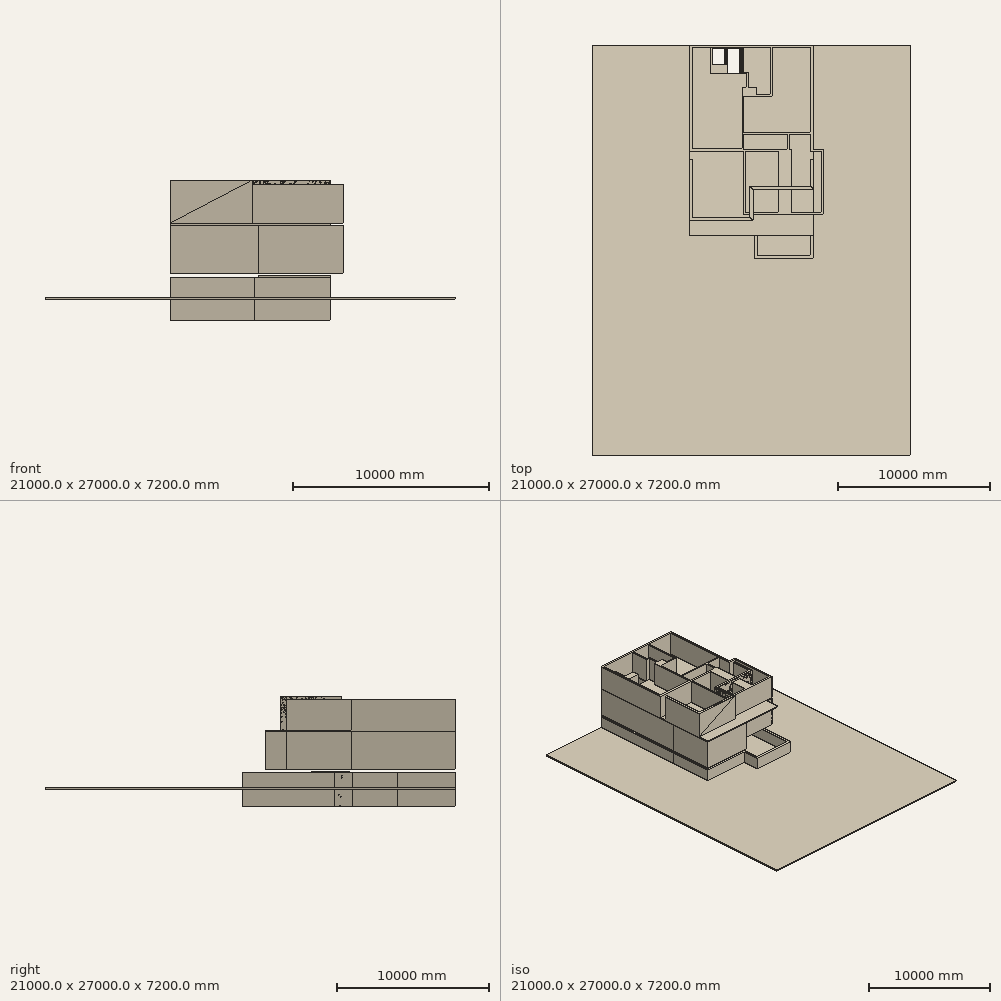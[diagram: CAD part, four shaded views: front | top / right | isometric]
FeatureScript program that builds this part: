
annotation { "Feature Type Name" : "Feature", "Feature Type Description" : "" }
export const myFeature = defineFeature(function(context is Context, id is Id, definition is map)
    precondition{}
    {
        {
            var Q0;
            Q0=qCreatedBy(makeId("Top.planeOp"),FACE);
            var sketch = newSketch(context, id + "F0", { "sketchPlane" : qUnion([Q0])});
            skLineSegment(sketch, "E0", {"start": v(-4100, -4250) * mm, "end": v(-4100, 4250) * mm});
            skLineSegment(sketch, "E1", {"start": v(-4100, 4250) * mm, "end": v(4100, 4250) * mm});
            skLineSegment(sketch, "E2", {"start": v(4100, 4250) * mm, "end": v(4100, -2750) * mm});
            skLineSegment(sketch, "E3", {"start": v(4100, -2750) * mm, "end": v(400, -2750) * mm});
            skLineSegment(sketch, "E4", {"start": v(400, -2750) * mm, "end": v(400, -4250) * mm});
            skLineSegment(sketch, "E5", {"start": v(400, -4250) * mm, "end": v(-4100, -4250) * mm});
            skLineSegment(sketch, "E6", {"start": v(-3950, -4100) * mm, "end": v(-3950, 4100) * mm});
            skLineSegment(sketch, "E7", {"start": v(-3950, 4100) * mm, "end": v(3900, 4100) * mm});
            skLineSegment(sketch, "E8", {"start": v(3900, 4100) * mm, "end": v(3900, -2600) * mm});
            skLineSegment(sketch, "E9", {"start": v(3900, -2600) * mm, "end": v(250, -2600) * mm});
            skLineSegment(sketch, "E10", {"start": v(250, -2600) * mm, "end": v(250, -4100) * mm});
            skLineSegment(sketch, "E11", {"start": v(250, -4100) * mm, "end": v(-3950, -4100) * mm});
            skLineSegment(sketch, "E12.bottom", {"start": v(-2750, 4100) * mm, "end": v(-2650, 4100) * mm});
            skLineSegment(sketch, "E12.top", {"start": v(-2750, 2100) * mm, "end": v(-2650, 2100) * mm});
            skLineSegment(sketch, "E12.left", {"start": v(-2750, 4100) * mm, "end": v(-2750, 2100) * mm});
            skLineSegment(sketch, "E12.right", {"start": v(-2650, 4100) * mm, "end": v(-2650, 2100) * mm});
            skLineSegment(sketch, "E13", {"start": v(-3950, 3300) * mm, "end": v(-2750, 3300) * mm});
            skLineSegment(sketch, "E14", {"start": v(-3950, 3200) * mm, "end": v(-2750, 3200) * mm});
            skLineSegment(sketch, "E15", {"start": v(-3950, 800) * mm, "end": v(-650, 800) * mm});
            skLineSegment(sketch, "E16", {"start": v(-650, 800) * mm, "end": v(-650, 2100) * mm});
            skLineSegment(sketch, "E17", {"start": v(-650, 2100) * mm, "end": v(-1650, 2100) * mm});
            skLineSegment(sketch, "E18", {"start": v(-1650, 2100) * mm, "end": v(-1650, 4100) * mm});
            skLineSegment(sketch, "E19", {"start": v(-1650, 4100) * mm, "end": v(-1550, 4100) * mm});
            skLineSegment(sketch, "E20", {"start": v(-1550, 4100) * mm, "end": v(-1550, 2200) * mm});
            skLineSegment(sketch, "E21", {"start": v(-1550, 2200) * mm, "end": v(-550, 2200) * mm});
            skLineSegment(sketch, "E22", {"start": v(-550, 2200) * mm, "end": v(-550, 700) * mm});
            skLineSegment(sketch, "E23", {"start": v(-550, 700) * mm, "end": v(-3950, 700) * mm});
            skLineSegment(sketch, "E24", {"start": v(-3950, 700) * mm, "end": v(-3950, 800) * mm});
            skLineSegment(sketch, "E25", {"start": v(-550, 2200) * mm, "end": v(-550, 4100) * mm});
            skLineSegment(sketch, "E26", {"start": v(-650, 4100) * mm, "end": v(-650, 2200) * mm});
            skLineSegment(sketch, "E27", {"start": v(-550, 700) * mm, "end": v(3900, 700) * mm});
            skLineSegment(sketch, "E28", {"start": v(3900, 800) * mm, "end": v(-550, 800) * mm});
            skLineSegment(sketch, "E29", {"start": v(-650, 700) * mm, "end": v(-650, 400) * mm});
            skLineSegment(sketch, "E30", {"start": v(-650, 400) * mm, "end": v(0, -200) * mm});
            skLineSegment(sketch, "E31", {"start": v(0, -200) * mm, "end": v(300, -200) * mm});
            skLineSegment(sketch, "E32", {"start": v(300, -200) * mm, "end": v(300, 0) * mm});
            skLineSegment(sketch, "E33", {"start": v(1800, 4100) * mm, "end": v(1800, 800) * mm});
            skLineSegment(sketch, "E34", {"start": v(1900, 4100) * mm, "end": v(1900, 800) * mm});
            skLineSegment(sketch, "E35", {"start": v(300, 0) * mm, "end": v(300, 1300) * mm});
            skLineSegment(sketch, "E36", {"start": v(300, 1300) * mm, "end": v(-550, 1300) * mm});
            skLineSegment(sketch, "E37", {"start": v(-550, -4250) * mm, "end": v(-550, -6900) * mm});
            skLineSegment(sketch, "E38", {"start": v(-550, -6900) * mm, "end": v(4750, -6900) * mm});
            skLineSegment(sketch, "E39", {"start": v(4750, -6900) * mm, "end": v(4750, -2600) * mm});
            skLineSegment(sketch, "E40", {"start": v(4750, -2600) * mm, "end": v(4100, -2600) * mm});
            skLineSegment(sketch, "E41", {"start": v(4100, -2750) * mm, "end": v(4600, -2750) * mm});
            skLineSegment(sketch, "E42", {"start": v(4600, -2750) * mm, "end": v(4600, -6750) * mm});
            skLineSegment(sketch, "E43", {"start": v(4600, -6750) * mm, "end": v(-400, -6750) * mm});
            skLineSegment(sketch, "E44", {"start": v(-400, -6750) * mm, "end": v(-400, -4250) * mm});
            skSolve(sketch);
        }
        {
            var Q0;
            Q0=makeQuery(id+"F0.imprint","IMPRINT",FACE,{"disambiguationData":[TD([[makeQuery(id+"F0.imprint","IMPRINT",EDGE,{"derivedFrom":sQuery(id+"F0.wireOp",EDGE,"E15")}),-1.0]])]});
            var Q1;
            {var subQ3=sQuery(id+"F0.wireOp",EDGE,"E36");Q1=makeQuery(id+"F0.imprint","IMPRINT",FACE,{"disambiguationData":[TD([[makeQuery(id+"F0.imprint","IMPRINT",EDGE,{"derivedFrom":subQ3}),1.0]])]});}
            var Q2;
            {var subQ1=sQuery(id+"F0.wireOp",EDGE,"E22");var subQ3=sQuery(id+"F0.wireOp",EDGE,"E28");var subQ4=makeQuery(id+"F0.imprint","INTERSECT",VERTEX,{"derivedFrom":[subQ1,subQ3]});Q2=makeQuery(id+"F0.imprint","IMPRINT",FACE,{"disambiguationData":[TD([[makeQuery(id+"F0.imprint","IMPRINT",EDGE,{"disambiguationData":[TD([[subQ4,1.0]])],"derivedFrom":subQ3}),1.0]])]});}
            var Q3;
            {var subQ0=sQuery(id+"F0.wireOp",EDGE,"E29");Q3=makeQuery(id+"F0.imprint","IMPRINT",FACE,{"disambiguationData":[TD([[makeQuery(id+"F0.imprint","IMPRINT",EDGE,{"derivedFrom":subQ0}),1.0]])]});}
            var Q4;
            {var subQ3=sQuery(id+"F0.wireOp",EDGE,"E8");var subQ6=sQuery(id+"F0.wireOp",EDGE,"E27");var subQ9=makeQuery(id+"F0.imprint","INTERSECT",VERTEX,{"derivedFrom":[subQ3,subQ6]});Q4=makeQuery(id+"F0.imprint","IMPRINT",FACE,{"disambiguationData":[TD([[makeQuery(id+"F0.imprint","IMPRINT",EDGE,{"disambiguationData":[TD([[subQ9,1.0]])],"derivedFrom":subQ3}),-1.0]])]});}
            var Q5;
            {var subQ0=sQuery(id+"F0.wireOp",EDGE,"E33");Q5=makeQuery(id+"F0.imprint","IMPRINT",FACE,{"disambiguationData":[TD([[makeQuery(id+"F0.imprint","IMPRINT",EDGE,{"derivedFrom":subQ0}),1.0]])]});}
            var Q6;
            Q6=makeQuery(id+"F0.imprint","IMPRINT",FACE,{"disambiguationData":[TD([[makeQuery(id+"F0.imprint","IMPRINT",EDGE,{"derivedFrom":sQuery(id+"F0.wireOp",EDGE,"E0")}),-1.0]])]});
            var Q7;
            {var subQ0=sQuery(id+"F0.wireOp",EDGE,"E13");Q7=makeQuery(id+"F0.imprint","IMPRINT",FACE,{"disambiguationData":[TD([[makeQuery(id+"F0.imprint","IMPRINT",EDGE,{"derivedFrom":subQ0}),-1.0]])]});}
            var Q8;
            {var subQ3=sQuery(id+"F0.wireOp",EDGE,"E12.bottom");Q8=makeQuery(id+"F0.imprint","IMPRINT",FACE,{"disambiguationData":[TD([[makeQuery(id+"F0.imprint","IMPRINT",EDGE,{"derivedFrom":subQ3}),-1.0]])]});}
            var Q9;
            {var subQ0=sQuery(id+"F0.wireOp",EDGE,"E25");Q9=makeQuery(id+"F0.imprint","IMPRINT",FACE,{"disambiguationData":[TD([[makeQuery(id+"F0.imprint","IMPRINT",EDGE,{"derivedFrom":subQ0}),1.0]])]});}
            var Q10;
            {var subQ0=sQuery(id+"F0.wireOp",EDGE,"E37");Q10=makeQuery(id+"F0.imprint","IMPRINT",FACE,{"disambiguationData":[TD([[makeQuery(id+"F0.imprint","IMPRINT",EDGE,{"derivedFrom":subQ0}),1.0]])]});}
            extrude(context, id + "F1", {"entities" : qUnion([Q0, Q1, Q2, Q3, Q4, Q5, Q6, Q7, Q8, Q9, Q10]), "depth" : 2500 * mm, "offsetDistance" : 25 * mm});
        }
        {
            var Q0;
            Q0=makeQuery(id+"F1.opExtrude","CAP_FACE",FACE,{"disambiguationData":[OSD([sQuery(id+"F0.wireOp",EDGE,"E0"),sQuery(id+"F0.wireOp",EDGE,"E1"),sQuery(id+"F0.wireOp",EDGE,"E2"),sQuery(id+"F0.wireOp",EDGE,"E3"),sQuery(id+"F0.wireOp",EDGE,"E4"),sQuery(id+"F0.wireOp",EDGE,"E5"),sQuery(id+"F0.wireOp",EDGE,"E6"),sQuery(id+"F0.wireOp",EDGE,"E7"),sQuery(id+"F0.wireOp",EDGE,"E8"),sQuery(id+"F0.wireOp",EDGE,"E9"),sQuery(id+"F0.wireOp",EDGE,"E10"),sQuery(id+"F0.wireOp",EDGE,"E11"),sQuery(id+"F0.wireOp",EDGE,"E12.top"),sQuery(id+"F0.wireOp",EDGE,"E12.left"),sQuery(id+"F0.wireOp",EDGE,"E12.right"),sQuery(id+"F0.wireOp",EDGE,"E13"),sQuery(id+"F0.wireOp",EDGE,"E14"),sQuery(id+"F0.wireOp",EDGE,"E15"),sQuery(id+"F0.wireOp",EDGE,"E16"),sQuery(id+"F0.wireOp",EDGE,"E17"),sQuery(id+"F0.wireOp",EDGE,"E18"),sQuery(id+"F0.wireOp",EDGE,"E20"),sQuery(id+"F0.wireOp",EDGE,"E21"),sQuery(id+"F0.wireOp",EDGE,"E22"),sQuery(id+"F0.wireOp",EDGE,"E23"),sQuery(id+"F0.wireOp",EDGE,"E25"),sQuery(id+"F0.wireOp",EDGE,"E26"),sQuery(id+"F0.wireOp",EDGE,"E27"),sQuery(id+"F0.wireOp",EDGE,"E28"),sQuery(id+"F0.wireOp",EDGE,"E29"),sQuery(id+"F0.wireOp",EDGE,"E30"),sQuery(id+"F0.wireOp",EDGE,"E31"),sQuery(id+"F0.wireOp",EDGE,"E32")])],"isStart":true});
            cPlane(context, id + "F2", {"entities" : qUnion([Q0]), "cplaneType" : CPlaneType.OFFSET, "offset" : 200 * mm, "width" : 150 * mm, "height" : 150 * mm});
        }
        {
            var Q0;
            Q0=qCreatedBy(id+"F2.planeOp",FACE);
            var sketch = newSketch(context, id + "F3", { "sketchPlane" : qUnion([Q0])});
            skLineSegment(sketch, "E45.bottom", {"start": v(400, 2750) * mm, "end": v(4100, 2750) * mm});
            skLineSegment(sketch, "E45.top", {"start": v(400, 5250) * mm, "end": v(4100, 5250) * mm});
            skLineSegment(sketch, "E45.left", {"start": v(400, 2750) * mm, "end": v(400, 5250) * mm});
            skLineSegment(sketch, "E45.right", {"start": v(4100, 2750) * mm, "end": v(4100, 5250) * mm});
            skSolve(sketch);
        }
        {
            var Q0;
            Q0=makeQuery(id+"F3.imprint","IMPRINT",FACE,{"disambiguationData":[TD([[makeQuery(id+"F3.imprint","IMPRINT",EDGE,{"derivedFrom":sQuery(id+"F3.wireOp",EDGE,"E45.bottom")}),1.0]])]});
            extrude(context, id + "F4", {"entities" : qUnion([Q0]), "oppositeDirection" : true, "depth" : 100 * mm, "offsetDistance" : 25 * mm});
        }
        {
            var Q0;
            Q0=makeQuery(id+"F1.opExtrude","CAP_FACE",FACE,{"disambiguationData":[OSD([sQuery(id+"F0.wireOp",EDGE,"E0"),sQuery(id+"F0.wireOp",EDGE,"E1"),sQuery(id+"F0.wireOp",EDGE,"E2"),sQuery(id+"F0.wireOp",EDGE,"E3"),sQuery(id+"F0.wireOp",EDGE,"E4"),sQuery(id+"F0.wireOp",EDGE,"E5"),sQuery(id+"F0.wireOp",EDGE,"E6"),sQuery(id+"F0.wireOp",EDGE,"E7"),sQuery(id+"F0.wireOp",EDGE,"E8"),sQuery(id+"F0.wireOp",EDGE,"E9"),sQuery(id+"F0.wireOp",EDGE,"E10"),sQuery(id+"F0.wireOp",EDGE,"E11"),sQuery(id+"F0.wireOp",EDGE,"E12.top"),sQuery(id+"F0.wireOp",EDGE,"E12.left"),sQuery(id+"F0.wireOp",EDGE,"E12.right"),sQuery(id+"F0.wireOp",EDGE,"E13"),sQuery(id+"F0.wireOp",EDGE,"E14"),sQuery(id+"F0.wireOp",EDGE,"E15"),sQuery(id+"F0.wireOp",EDGE,"E16"),sQuery(id+"F0.wireOp",EDGE,"E17"),sQuery(id+"F0.wireOp",EDGE,"E18"),sQuery(id+"F0.wireOp",EDGE,"E20"),sQuery(id+"F0.wireOp",EDGE,"E21"),sQuery(id+"F0.wireOp",EDGE,"E22"),sQuery(id+"F0.wireOp",EDGE,"E23"),sQuery(id+"F0.wireOp",EDGE,"E25"),sQuery(id+"F0.wireOp",EDGE,"E26"),sQuery(id+"F0.wireOp",EDGE,"E27"),sQuery(id+"F0.wireOp",EDGE,"E28"),sQuery(id+"F0.wireOp",EDGE,"E29"),sQuery(id+"F0.wireOp",EDGE,"E30"),sQuery(id+"F0.wireOp",EDGE,"E31"),sQuery(id+"F0.wireOp",EDGE,"E32")])],"isStart":false});
            cPlane(context, id + "F5", {"entities" : qUnion([Q0]), "cplaneType" : CPlaneType.OFFSET, "offset" : 0 * mm, "width" : 150 * mm, "height" : 150 * mm});
        }
        {
            var Q0;
            Q0=qCreatedBy(id+"F5.planeOp",FACE);
            var sketch = newSketch(context, id + "F6", { "sketchPlane" : qUnion([Q0])});
            skLineSegment(sketch, "E46.bottom", {"start": v(-4100, 4250) * mm, "end": v(4100, 4250) * mm});
            skLineSegment(sketch, "E46.top", {"start": v(-4100, -4450) * mm, "end": v(4100, -4450) * mm});
            skLineSegment(sketch, "E46.left", {"start": v(-4100, 4250) * mm, "end": v(-4100, -4450) * mm});
            skLineSegment(sketch, "E46.right", {"start": v(4100, 4250) * mm, "end": v(4100, -4450) * mm});
            skLineSegment(sketch, "E47.bottom", {"start": v(-2600, 4100) * mm, "end": v(-600, 4100) * mm});
            skLineSegment(sketch, "E47.top", {"start": v(-2600, 2400) * mm, "end": v(-600, 2400) * mm});
            skLineSegment(sketch, "E47.left", {"start": v(-2600, 4100) * mm, "end": v(-2600, 2400) * mm});
            skLineSegment(sketch, "E47.right", {"start": v(-600, 4100) * mm, "end": v(-600, 2400) * mm});
            skSolve(sketch);
        }
        {
            var Q0;
            Q0=makeQuery(id+"F6.imprint","IMPRINT",FACE,{"disambiguationData":[TD([[makeQuery(id+"F6.imprint","IMPRINT",EDGE,{"derivedFrom":sQuery(id+"F6.wireOp",EDGE,"E46.bottom")}),-1.0]])]});
            extrude(context, id + "F7", {"entities" : qUnion([Q0]), "depth" : 100 * mm, "offsetDistance" : 25 * mm});
        }
        {
            var Q0;
            Q0=makeQuery(id+"F7.opExtrude","CAP_FACE",FACE,{"disambiguationData":[OSD([sQuery(id+"F6.wireOp",EDGE,"E46.bottom"),sQuery(id+"F6.wireOp",EDGE,"E46.top"),sQuery(id+"F6.wireOp",EDGE,"E46.left"),sQuery(id+"F6.wireOp",EDGE,"E46.right")])],"isStart":false});
            var sketch = newSketch(context, id + "F8", { "sketchPlane" : qUnion([Q0])});
            skLineSegment(sketch, "E48", {"start": v(-4100, -2750) * mm, "end": v(-400, -2750) * mm});
            skLineSegment(sketch, "E49", {"start": v(-2600, 4100) * mm, "end": v(-3900, 4100) * mm});
            skLineSegment(sketch, "E50", {"start": v(-3900, 4100) * mm, "end": v(-3900, -2550) * mm});
            skLineSegment(sketch, "E51", {"start": v(-3900, -2550) * mm, "end": v(-500, -2550) * mm});
            skLineSegment(sketch, "E52", {"start": v(3900, -2550) * mm, "end": v(3900, 4100) * mm});
            skLineSegment(sketch, "E53", {"start": v(3900, 4100) * mm, "end": v(-2600, 4100) * mm});
            skLineSegment(sketch, "E54", {"start": v(-2700, 4100) * mm, "end": v(-2700, 2500) * mm});
            skLineSegment(sketch, "E55", {"start": v(-2700, 2500) * mm, "end": v(-3900, 2500) * mm});
            skLineSegment(sketch, "E56", {"start": v(-3900, 2500) * mm, "end": v(-3900, 2400) * mm});
            skLineSegment(sketch, "E57", {"start": v(-3900, 2400) * mm, "end": v(-2600, 2400) * mm});
            skLineSegment(sketch, "E58", {"start": v(-2600, 2400) * mm, "end": v(-2600, 4100) * mm});
            skLineSegment(sketch, "E59", {"start": v(-2600, 4100) * mm, "end": v(-2700, 4100) * mm});
            skLineSegment(sketch, "E60", {"start": v(-600, 4100) * mm, "end": v(-600, 2400) * mm});
            skLineSegment(sketch, "E61", {"start": v(-600, 2400) * mm, "end": v(1350, 2400) * mm});
            skLineSegment(sketch, "E62", {"start": v(1350, 2400) * mm, "end": v(1350, 4100) * mm});
            skLineSegment(sketch, "E63", {"start": v(1350, 4100) * mm, "end": v(-600, 4100) * mm});
            skLineSegment(sketch, "E64", {"start": v(-500, 4100) * mm, "end": v(-500, 2500) * mm});
            skLineSegment(sketch, "E65", {"start": v(-500, 2500) * mm, "end": v(1250, 2500) * mm});
            skLineSegment(sketch, "E66", {"start": v(1250, 2500) * mm, "end": v(1250, 4100) * mm});
            skLineSegment(sketch, "E67", {"start": v(1350, 2400) * mm, "end": v(1350, 1000) * mm});
            skLineSegment(sketch, "E68", {"start": v(1350, 1000) * mm, "end": v(3900, 1000) * mm});
            skLineSegment(sketch, "E69", {"start": v(3900, 1000) * mm, "end": v(3900, 900) * mm});
            skLineSegment(sketch, "E70", {"start": v(3900, 900) * mm, "end": v(1250, 900) * mm});
            skLineSegment(sketch, "E71", {"start": v(1250, 900) * mm, "end": v(1250, 2400) * mm});
            skLineSegment(sketch, "E72", {"start": v(1250, 2400) * mm, "end": v(1350, 2400) * mm});
            skLineSegment(sketch, "E73", {"start": v(1250, 900) * mm, "end": v(-500, 900) * mm});
            skLineSegment(sketch, "E74", {"start": v(-500, 900) * mm, "end": v(-500, -2550) * mm});
            skLineSegment(sketch, "E75", {"start": v(-500, -2550) * mm, "end": v(-600, -2550) * mm});
            skLineSegment(sketch, "E76", {"start": v(-600, -2550) * mm, "end": v(-600, 1000) * mm});
            skLineSegment(sketch, "E77", {"start": v(-600, 1000) * mm, "end": v(1250, 1000) * mm});
            skLineSegment(sketch, "E78", {"start": v(1250, 1000) * mm, "end": v(1250, 900) * mm});
            skLineSegment(sketch, "E79", {"start": v(-3900, -440) * mm, "end": v(-3900, -340) * mm});
            skLineSegment(sketch, "E80", {"start": v(-2600, 2400) * mm, "end": v(-1600, 2400) * mm});
            skLineSegment(sketch, "E81", {"start": v(-4100, -2750) * mm, "end": v(-4100, 4250) * mm});
            skLineSegment(sketch, "E82", {"start": v(-4100, 4250) * mm, "end": v(4100, 4250) * mm});
            skLineSegment(sketch, "E83", {"start": v(4100, 4250) * mm, "end": v(4100, -2750) * mm});
            skLineSegment(sketch, "E84", {"start": v(-1600, 2400) * mm, "end": v(-1600, 3000) * mm});
            skLineSegment(sketch, "E85", {"start": v(-1600, 3000) * mm, "end": v(-2600, 3000) * mm});
            skLineSegment(sketch, "E86", {"start": v(-600, 1000) * mm, "end": v(-600, 1500) * mm});
            skLineSegment(sketch, "E87", {"start": v(-600, 1500) * mm, "end": v(350, 1500) * mm});
            skLineSegment(sketch, "E88", {"start": v(350, 1500) * mm, "end": v(350, 1000) * mm});
            skPoint(sketch, "E89.endSnap0", {"position": v(375, 900) * mm});
            skLineSegment(sketch, "E90", {"start": v(4100, -2750) * mm, "end": v(4600, -2750) * mm});
            skLineSegment(sketch, "E91", {"start": v(4600, -2750) * mm, "end": v(4600, -6750) * mm});
            skLineSegment(sketch, "E92", {"start": v(4600, -6750) * mm, "end": v(-400, -6750) * mm});
            skLineSegment(sketch, "E93", {"start": v(-400, -6750) * mm, "end": v(-400, -2750) * mm});
            skLineSegment(sketch, "E94", {"start": v(-550, -6900) * mm, "end": v(4750, -6900) * mm});
            skLineSegment(sketch, "E95", {"start": v(4750, -6900) * mm, "end": v(4750, -2600) * mm});
            skLineSegment(sketch, "E96", {"start": v(4750, -2600) * mm, "end": v(4100, -2600) * mm});
            skLineSegment(sketch, "E97", {"start": v(4100, -2600) * mm, "end": v(4100, -2750) * mm});
            skLineSegment(sketch, "E98", {"start": v(-550, -6900) * mm, "end": v(-550, -2750) * mm});
            skLineSegment(sketch, "E99", {"start": v(1750, -6750) * mm, "end": v(1750, -2600) * mm});
            skLineSegment(sketch, "E100", {"start": v(2650, -2600) * mm, "end": v(2650, -6750) * mm});
            skLineSegment(sketch, "E101", {"start": v(3900, -1600) * mm, "end": v(-500, -1600) * mm});
            skLineSegment(sketch, "E102", {"start": v(-500, -1450) * mm, "end": v(3900, -1450) * mm});
            skLineSegment(sketch, "E103", {"start": v(2200, -6750) * mm, "end": v(2200, -2600) * mm});
            skLineSegment(sketch, "E104", {"start": v(1750, -2600) * mm, "end": v(2650, -2600) * mm});
            skLineSegment(sketch, "E105", {"start": v(3900, -2550) * mm, "end": v(3900, -2750) * mm});
            skLineSegment(sketch, "E106", {"start": v(3900, -2750) * mm, "end": v(4100, -2750) * mm});
            skLineSegment(sketch, "E107", {"start": v(-500, -2550) * mm, "end": v(-500, -2750) * mm});
            skLineSegment(sketch, "E108", {"start": v(-400, -2750) * mm, "end": v(1750, -2750) * mm});
            skLineSegment(sketch, "E109", {"start": v(1750, -2600) * mm, "end": v(-500, -2600) * mm});
            skLineSegment(sketch, "E110", {"start": v(2377.07, -1600) * mm, "end": v(2377.07, -2600) * mm});
            skLineSegment(sketch, "E111", {"start": v(2527.07, -1600) * mm, "end": v(2527.07, -2600) * mm});
            skLineSegment(sketch, "E112", {"start": v(1350, 1000) * mm, "end": v(1350, 900) * mm});
            skLineSegment(sketch, "E113", {"start": v(-300, 2400) * mm, "end": v(-300, 1500) * mm});
            skLineSegment(sketch, "E114", {"start": v(-200, 2400) * mm, "end": v(-200, 1500) * mm});
            skLineSegment(sketch, "E115", {"start": v(1250, 2500) * mm, "end": v(1250, 2400) * mm});
            skLineSegment(sketch, "E116", {"start": v(-500, 2500) * mm, "end": v(-500, 2400) * mm});
            skLineSegment(sketch, "E117", {"start": v(-200, 2400) * mm, "end": v(-200, 2500) * mm});
            skLineSegment(sketch, "E118", {"start": v(-2700, 2500) * mm, "end": v(-2700, 2400) * mm});
            skSolve(sketch);
        }
        {
            var Q0;
            {var subQ18=sQuery(id+"F8.wireOp",EDGE,"E49");Q0=makeQuery(id+"F8.imprint","IMPRINT",FACE,{"disambiguationData":[TD([[makeQuery(id+"F8.imprint","IMPRINT",EDGE,{"derivedFrom":subQ18}),-1.0]])]});}
            var Q1;
            Q1=makeQuery(id+"F8.imprint","IMPRINT",FACE,{"disambiguationData":[TD([[makeQuery(id+"F8.imprint","IMPRINT",EDGE,{"derivedFrom":sQuery(id+"F8.wireOp",EDGE,"E90")}),1.0]])]});
            var Q2;
            {var subQ1=sQuery(id+"F8.wireOp",EDGE,"E48");var subQ3=sQuery(id+"F8.wireOp",EDGE,"E98");var subQ4=makeQuery(id+"F8.imprint","INTERSECT",VERTEX,{"derivedFrom":[subQ1,subQ3]});Q2=makeQuery(id+"F8.imprint","IMPRINT",FACE,{"disambiguationData":[TD([[makeQuery(id+"F8.imprint","IMPRINT",EDGE,{"disambiguationData":[TD([[subQ4,1.0]])],"derivedFrom":subQ3}),-1.0]])]});}
            var Q3;
            {var subQ2=sQuery(id+"F8.wireOp",EDGE,"E108");Q3=makeQuery(id+"F8.imprint","IMPRINT",FACE,{"disambiguationData":[TD([[makeQuery(id+"F8.imprint","IMPRINT",EDGE,{"derivedFrom":subQ2}),1.0]])]});}
            var Q4;
            {var subQ1=sQuery(id+"F8.wireOp",EDGE,"E99");var subQ5=makeQuery(id+"F8.imprint","INTERSECT",VERTEX,{"derivedFrom":[subQ1,sQuery(id+"F8.wireOp",EDGE,"E108")]});Q4=makeQuery(id+"F8.imprint","IMPRINT",FACE,{"disambiguationData":[TD([[makeQuery(id+"F8.imprint","IMPRINT",EDGE,{"disambiguationData":[TD([[subQ5,1.0]])],"derivedFrom":subQ1}),-1.0]])]});}
            var Q5;
            {var subQ0=sQuery(id+"F8.wireOp",EDGE,"E104");var subQ1=sQuery(id+"F8.wireOp",EDGE,"E100");var subQ2=makeQuery(id+"F8.imprint","INTERSECT",VERTEX,{"derivedFrom":[subQ1,subQ0]});Q5=makeQuery(id+"F8.imprint","IMPRINT",FACE,{"disambiguationData":[TD([[makeQuery(id+"F8.imprint","IMPRINT",EDGE,{"disambiguationData":[TD([[subQ2,-1.0]])],"derivedFrom":subQ1}),-1.0]])]});}
            var Q6;
            {var subQ0=sQuery(id+"F8.wireOp",EDGE,"E99");var subQ1=sQuery(id+"F8.wireOp",EDGE,"E92");var subQ2=makeQuery(id+"F8.imprint","INTERSECT",VERTEX,{"derivedFrom":[subQ1,subQ0]});Q6=makeQuery(id+"F8.imprint","IMPRINT",FACE,{"disambiguationData":[TD([[makeQuery(id+"F8.imprint","IMPRINT",EDGE,{"disambiguationData":[TD([[subQ2,1.0]])],"derivedFrom":subQ1}),-1.0]])]});}
            var Q7;
            {var subQ0=sQuery(id+"F8.wireOp",EDGE,"E100");var subQ1=sQuery(id+"F8.wireOp",EDGE,"E92");var subQ2=makeQuery(id+"F8.imprint","INTERSECT",VERTEX,{"derivedFrom":[subQ1,subQ0]});Q7=makeQuery(id+"F8.imprint","IMPRINT",FACE,{"disambiguationData":[TD([[makeQuery(id+"F8.imprint","IMPRINT",EDGE,{"disambiguationData":[TD([[subQ2,-1.0]])],"derivedFrom":subQ1}),-1.0]])]});}
            var Q8;
            {var subQ4=sQuery(id+"F8.wireOp",EDGE,"E73");Q8=makeQuery(id+"F8.imprint","IMPRINT",FACE,{"disambiguationData":[TD([[makeQuery(id+"F8.imprint","IMPRINT",EDGE,{"derivedFrom":subQ4}),-1.0]])]});}
            var Q9;
            {var subQ5=sQuery(id+"F8.wireOp",EDGE,"E102");Q9=makeQuery(id+"F8.imprint","IMPRINT",FACE,{"disambiguationData":[TD([[makeQuery(id+"F8.imprint","IMPRINT",EDGE,{"derivedFrom":subQ5}),-1.0]])]});}
            var Q10;
            {var subQ0=sQuery(id+"F8.wireOp",EDGE,"E110");Q10=makeQuery(id+"F8.imprint","IMPRINT",FACE,{"disambiguationData":[TD([[makeQuery(id+"F8.imprint","IMPRINT",EDGE,{"derivedFrom":subQ0}),1.0]])]});}
            var Q11;
            Q11=makeQuery(id+"F8.imprint","IMPRINT",FACE,{"disambiguationData":[TD([[makeQuery(id+"F8.imprint","IMPRINT",EDGE,{"derivedFrom":sQuery(id+"F8.wireOp",EDGE,"E67")}),-1.0]])]});
            var Q12;
            {var subQ2=sQuery(id+"F8.wireOp",EDGE,"E60");Q12=makeQuery(id+"F8.imprint","IMPRINT",FACE,{"disambiguationData":[TD([[makeQuery(id+"F8.imprint","IMPRINT",EDGE,{"derivedFrom":subQ2}),1.0]])]});}
            var Q13;
            {var subQ0=sQuery(id+"F8.wireOp",EDGE,"E113");Q13=makeQuery(id+"F8.imprint","IMPRINT",FACE,{"disambiguationData":[TD([[makeQuery(id+"F8.imprint","IMPRINT",EDGE,{"derivedFrom":subQ0}),1.0]])]});}
            var Q14;
            {var subQ3=sQuery(id+"F8.wireOp",EDGE,"E86");Q14=makeQuery(id+"F8.imprint","IMPRINT",FACE,{"disambiguationData":[TD([[makeQuery(id+"F8.imprint","IMPRINT",EDGE,{"derivedFrom":subQ3}),-1.0]])]});}
            var Q15;
            {var subQ0=sQuery(id+"F8.wireOp",EDGE,"E116");Q15=makeQuery(id+"F8.imprint","IMPRINT",FACE,{"disambiguationData":[TD([[makeQuery(id+"F8.imprint","IMPRINT",EDGE,{"derivedFrom":subQ0}),1.0]])]});}
            var Q16;
            {var subQ2=sQuery(id+"F8.wireOp",EDGE,"E62");Q16=makeQuery(id+"F8.imprint","IMPRINT",FACE,{"disambiguationData":[TD([[makeQuery(id+"F8.imprint","IMPRINT",EDGE,{"derivedFrom":subQ2}),1.0]])]});}
            extrude(context, id + "F9", {"entities" : qUnion([Q0, Q1, Q2, Q3, Q4, Q5, Q6, Q7, Q8, Q9, Q10, Q11, Q12, Q13, Q14, Q15, Q16]), "operationType" : NewBodyOperationType.ADD, "depth" : 2000 * mm, "offsetDistance" : 25 * mm});
        }
        {
            var Q0;
            Q0=qCreatedBy(id+"F2.planeOp",FACE);
            cPlane(context, id + "F10", {"entities" : qUnion([Q0]), "cplaneType" : CPlaneType.OFFSET, "offset" : 2200 * mm, "width" : 150 * mm, "height" : 150 * mm});
        }
        {
            var Q0;
            Q0=qCreatedBy(id+"F10.planeOp",FACE);
            var sketch = newSketch(context, id + "F11", { "sketchPlane" : qUnion([Q0])});
            skLineSegment(sketch, "E119.bottom", {"start": v(-4100, -4250) * mm, "end": v(4100, -4250) * mm});
            skLineSegment(sketch, "E119.top", {"start": v(400, 2750) * mm, "end": v(2600, 2750) * mm});
            skLineSegment(sketch, "E119.left", {"start": v(-4100, -4250) * mm, "end": v(-4100, 2750) * mm});
            skLineSegment(sketch, "E119.right", {"start": v(4100, -4250) * mm, "end": v(4100, -450) * mm});
            skLineSegment(sketch, "E120", {"start": v(4100, -450) * mm, "end": v(2600, -450) * mm});
            skLineSegment(sketch, "E121", {"start": v(2600, -450) * mm, "end": v(2600, 2750) * mm});
            skLineSegment(sketch, "E122", {"start": v(-3900, -4050) * mm, "end": v(3900, -4050) * mm});
            skLineSegment(sketch, "E123", {"start": v(3900, -4050) * mm, "end": v(3900, -750) * mm});
            skLineSegment(sketch, "E124", {"start": v(3900, -750) * mm, "end": v(2300, -750) * mm});
            skLineSegment(sketch, "E125", {"start": v(2300, -750) * mm, "end": v(2300, 2550) * mm});
            skLineSegment(sketch, "E126", {"start": v(400, 2750) * mm, "end": v(400, 4250) * mm});
            skLineSegment(sketch, "E127", {"start": v(400, 4250) * mm, "end": v(-4100, 4250) * mm});
            skLineSegment(sketch, "E128", {"start": v(-4100, 4250) * mm, "end": v(-4100, 2750) * mm});
            skLineSegment(sketch, "E129", {"start": v(200, 2550) * mm, "end": v(200, 4050) * mm});
            skLineSegment(sketch, "E130", {"start": v(200, 4050) * mm, "end": v(-3900, 4050) * mm});
            skLineSegment(sketch, "E131", {"start": v(-3900, 4050) * mm, "end": v(-3900, -4050) * mm});
            skLineSegment(sketch, "E132", {"start": v(200, 2550) * mm, "end": v(-3900, 2550) * mm});
            skLineSegment(sketch, "E133", {"start": v(200, 2750) * mm, "end": v(-3900, 2750) * mm});
            skLineSegment(sketch, "E134.trimOffspring", {"start": v(2300, 2550) * mm, "end": v(200, 2550) * mm});
            skLineSegment(sketch, "E135", {"start": v(2600, 2550) * mm, "end": v(4100, 2550) * mm});
            skLineSegment(sketch, "E136", {"start": v(4100, 2550) * mm, "end": v(4100, 3750) * mm});
            skLineSegment(sketch, "E137", {"start": v(4100, 3750) * mm, "end": v(2600, 3750) * mm});
            skLineSegment(sketch, "E138", {"start": v(2600, 3750) * mm, "end": v(2600, 2750) * mm});
            skLineSegment(sketch, "E139.bottom", {"start": v(2800, 2750) * mm, "end": v(3900, 2750) * mm});
            skLineSegment(sketch, "E139.top", {"start": v(2800, 3550) * mm, "end": v(3900, 3550) * mm});
            skLineSegment(sketch, "E139.left", {"start": v(2800, 2750) * mm, "end": v(2800, 3550) * mm});
            skLineSegment(sketch, "E139.right", {"start": v(3900, 2750) * mm, "end": v(3900, 3550) * mm});
            skLineSegment(sketch, "E140", {"start": v(2300, -750) * mm, "end": v(-3900, -750) * mm});
            skLineSegment(sketch, "E141", {"start": v(-3900, -500) * mm, "end": v(2300, -500) * mm});
            skLineSegment(sketch, "E142", {"start": v(-700, -4050) * mm, "end": v(-700, -750) * mm});
            skLineSegment(sketch, "E143", {"start": v(-800, -4050) * mm, "end": v(-800, -750) * mm});
            skLineSegment(sketch, "E144", {"start": v(2000, -4050) * mm, "end": v(2000, -750) * mm});
            skLineSegment(sketch, "E145", {"start": v(1900, -4050) * mm, "end": v(1900, -750) * mm});
            skLineSegment(sketch, "E146", {"start": v(-2800, -4050) * mm, "end": v(-2800, -2200) * mm});
            skLineSegment(sketch, "E147", {"start": v(-2800, -2200) * mm, "end": v(-3900, -2200) * mm});
            skLineSegment(sketch, "E148", {"start": v(-2900, -4050) * mm, "end": v(-2900, -2300) * mm});
            skLineSegment(sketch, "E149", {"start": v(-2900, -2300) * mm, "end": v(-3900, -2300) * mm});
            skLineSegment(sketch, "E150", {"start": v(-1800, -4050) * mm, "end": v(-1800, -2200) * mm});
            skLineSegment(sketch, "E151", {"start": v(-1800, -2200) * mm, "end": v(-800, -2200) * mm});
            skLineSegment(sketch, "E152", {"start": v(-1700, -4050) * mm, "end": v(-1700, -2300) * mm});
            skLineSegment(sketch, "E153", {"start": v(-1700, -2300) * mm, "end": v(-800, -2300) * mm});
            skSolve(sketch);
        }
        {
            var Q0;
            Q0=makeQuery(id+"F11.imprint","IMPRINT",FACE,{"disambiguationData":[TD([[makeQuery(id+"F11.imprint","IMPRINT",EDGE,{"derivedFrom":sQuery(id+"F11.wireOp",EDGE,"E119.bottom")}),1.0]])]});
            var Q1;
            {var subQ0=sQuery(id+"F11.wireOp",EDGE,"E132");Q1=makeQuery(id+"F11.imprint","IMPRINT",FACE,{"disambiguationData":[TD([[makeQuery(id+"F11.imprint","IMPRINT",EDGE,{"derivedFrom":subQ0}),-1.0]])]});}
            var Q2;
            {var subQ7=sQuery(id+"F11.wireOp",EDGE,"E141");Q2=makeQuery(id+"F11.imprint","IMPRINT",FACE,{"disambiguationData":[TD([[makeQuery(id+"F11.imprint","IMPRINT",EDGE,{"derivedFrom":subQ7}),-1.0]])]});}
            var Q3;
            {var subQ0=sQuery(id+"F11.wireOp",EDGE,"E144");Q3=makeQuery(id+"F11.imprint","IMPRINT",FACE,{"disambiguationData":[TD([[makeQuery(id+"F11.imprint","IMPRINT",EDGE,{"derivedFrom":subQ0}),1.0]])]});}
            var Q4;
            {var subQ0=sQuery(id+"F11.wireOp",EDGE,"E142");Q4=makeQuery(id+"F11.imprint","IMPRINT",FACE,{"disambiguationData":[TD([[makeQuery(id+"F11.imprint","IMPRINT",EDGE,{"derivedFrom":subQ0}),1.0]])]});}
            var Q5;
            {var subQ0=sQuery(id+"F11.wireOp",EDGE,"E146");Q5=makeQuery(id+"F11.imprint","IMPRINT",FACE,{"disambiguationData":[TD([[makeQuery(id+"F11.imprint","IMPRINT",EDGE,{"derivedFrom":subQ0}),1.0]])]});}
            var Q6;
            {var subQ0=sQuery(id+"F11.wireOp",EDGE,"E135");Q6=makeQuery(id+"F11.imprint","IMPRINT",FACE,{"disambiguationData":[TD([[makeQuery(id+"F11.imprint","IMPRINT",EDGE,{"derivedFrom":subQ0}),1.0]])]});}
            var Q7;
            {var subQ3=sQuery(id+"F11.wireOp",EDGE,"E150");Q7=makeQuery(id+"F11.imprint","IMPRINT",FACE,{"disambiguationData":[TD([[makeQuery(id+"F11.imprint","IMPRINT",EDGE,{"derivedFrom":subQ3}),-1.0]])]});}
            extrude(context, id + "F12", {"entities" : qUnion([Q0, Q1, Q2, Q3, Q4, Q5, Q6, Q7]), "oppositeDirection" : true, "depth" : 2200 * mm, "offsetDistance" : 25 * mm});
        }
        {
            var Q0;
            {var subQ0=sQuery(id+"F8.wireOp",EDGE,"E80");Q0=makeQuery(id+"F8.imprint","IMPRINT",FACE,{"disambiguationData":[TD([[makeQuery(id+"F8.imprint","IMPRINT",EDGE,{"derivedFrom":subQ0}),1.0]])]});}
            var Q1;
            Q1=makeQuery(id+"F8.imprint","IMPRINT",FACE,{"disambiguationData":[TD([[makeQuery(id+"F8.imprint","IMPRINT",EDGE,{"derivedFrom":sQuery(id+"F8.wireOp",EDGE,"E54")}),1.0]])]});
            extrude(context, id + "F13", {"entities" : qUnion([Q0, Q1]), "operationType" : NewBodyOperationType.ADD, "depth" : 1000 * mm, "offsetDistance" : 25 * mm, "hasSecondDirection" : true, "secondDirectionOppositeDirection" : true, "secondDirectionDepth" : 25 * mm});
        }
        {
            var Q0;
            Q0=qCreatedBy(id+"F10.planeOp",FACE);
            var sketch = newSketch(context, id + "F14", { "sketchPlane" : qUnion([Q0])});
            skLineSegment(sketch, "E154", {"start": v(-4100, 4250) * mm, "end": v(-4100, 8250) * mm});
            skLineSegment(sketch, "E155", {"start": v(-4100, 8250) * mm, "end": v(200, 8250) * mm});
            skLineSegment(sketch, "E156", {"start": v(200, 8250) * mm, "end": v(200, 9750) * mm});
            skLineSegment(sketch, "E157", {"start": v(200, 9750) * mm, "end": v(4100, 9750) * mm});
            skLineSegment(sketch, "E158", {"start": v(4100, 9750) * mm, "end": v(4100, 2750) * mm});
            skLineSegment(sketch, "E159", {"start": v(4100, 2750) * mm, "end": v(3900, 2750) * mm});
            skLineSegment(sketch, "E160", {"start": v(3900, 2750) * mm, "end": v(3900, 9550) * mm});
            skLineSegment(sketch, "E161", {"start": v(3900, 9550) * mm, "end": v(400, 9550) * mm});
            skLineSegment(sketch, "E162", {"start": v(400, 9550) * mm, "end": v(400, 8050) * mm});
            skLineSegment(sketch, "E163", {"start": v(400, 8050) * mm, "end": v(-3900, 8050) * mm});
            skLineSegment(sketch, "E164", {"start": v(-3900, 8050) * mm, "end": v(-3900, 4250) * mm});
            skLineSegment(sketch, "E165", {"start": v(-3900, 4250) * mm, "end": v(-4100, 4250) * mm});
            skSolve(sketch);
        }
        {
            var Q0;
            Q0=makeQuery(id+"F14.imprint","IMPRINT",FACE,{"disambiguationData":[TD([[makeQuery(id+"F14.imprint","IMPRINT",EDGE,{"derivedFrom":sQuery(id+"F14.wireOp",EDGE,"E154")}),-1.0]])]});
            extrude(context, id + "F15", {"entities" : qUnion([Q0]), "oppositeDirection" : true, "depth" : 2200 * mm, "offsetDistance" : 25 * mm});
        }
        {
            var Q0;
            Q0=qCreatedBy(makeId("Top.planeOp"),FACE);
            var sketch = newSketch(context, id + "F16", { "sketchPlane" : qUnion([Q0])});
            skLineSegment(sketch, "E166", {"start": v(-4100, -4250) * mm, "end": v(-4100, -8250) * mm});
            skLineSegment(sketch, "E167", {"start": v(-4100, -8250) * mm, "end": v(400, -8250) * mm});
            skLineSegment(sketch, "E168", {"start": v(400, -8250) * mm, "end": v(400, -6750) * mm});
            skLineSegment(sketch, "E169", {"start": v(400, -6750) * mm, "end": v(4100, -6750) * mm});
            skLineSegment(sketch, "E170", {"start": v(4100, -6750) * mm, "end": v(4100, -2750) * mm});
            skLineSegment(sketch, "E171", {"start": v(4100, -2750) * mm, "end": v(3900, -2750) * mm});
            skLineSegment(sketch, "E172", {"start": v(3900, -2750) * mm, "end": v(3900, -6550) * mm});
            skLineSegment(sketch, "E173", {"start": v(3900, -6550) * mm, "end": v(200, -6550) * mm});
            skLineSegment(sketch, "E174", {"start": v(200, -6550) * mm, "end": v(200, -8050) * mm});
            skLineSegment(sketch, "E175", {"start": v(200, -8050) * mm, "end": v(-3900, -8050) * mm});
            skLineSegment(sketch, "E176", {"start": v(-3900, -8050) * mm, "end": v(-3900, -4250) * mm});
            skLineSegment(sketch, "E177", {"start": v(-3900, -4250) * mm, "end": v(-4100, -4250) * mm});
            skSolve(sketch);
        }
        {
            var Q0;
            Q0=makeQuery(id+"F16.imprint","IMPRINT",FACE,{"disambiguationData":[TD([[makeQuery(id+"F16.imprint","IMPRINT",EDGE,{"derivedFrom":sQuery(id+"F16.wireOp",EDGE,"E166")}),1.0]])]});
            extrude(context, id + "F17", {"entities" : qUnion([Q0]), "depth" : 2500 * mm, "offsetDistance" : 25 * mm});
        }
        {
            var Q0;
            Q0=qCreatedBy(id+"F5.planeOp",FACE);
            var sketch = newSketch(context, id + "F18", { "sketchPlane" : qUnion([Q0])});
            skLineSegment(sketch, "E178", {"start": v(-4100, -4450) * mm, "end": v(-4100, -8250) * mm});
            skLineSegment(sketch, "E179", {"start": v(-4100, -8250) * mm, "end": v(4100, -8250) * mm});
            skLineSegment(sketch, "E180", {"start": v(4100, -8250) * mm, "end": v(4100, -4450) * mm});
            skLineSegment(sketch, "E181", {"start": v(4100, -4450) * mm, "end": v(-4100, -4450) * mm});
            skSolve(sketch);
        }
        {
            var Q0;
            Q0=makeQuery(id+"F18.imprint","IMPRINT",FACE,{"disambiguationData":[TD([[makeQuery(id+"F18.imprint","IMPRINT",EDGE,{"derivedFrom":sQuery(id+"F18.wireOp",EDGE,"E178")}),1.0]])]});
            extrude(context, id + "F19", {"entities" : qUnion([Q0]), "depth" : 100 * mm, "offsetDistance" : 25 * mm});
        }
        {
            var Q0;
            Q0=makeQuery(id+"F19.opExtrude","CAP_FACE",FACE,{"disambiguationData":[OSD([sQuery(id+"F18.wireOp",EDGE,"E178"),sQuery(id+"F18.wireOp",EDGE,"E179"),sQuery(id+"F18.wireOp",EDGE,"E180"),sQuery(id+"F18.wireOp",EDGE,"E181")])],"isStart":false});
            var sketch = newSketch(context, id + "F20", { "sketchPlane" : qUnion([Q0])});
            skLineSegment(sketch, "E182", {"start": v(-4100, -3250) * mm, "end": v(-4100, -7250) * mm});
            skLineSegment(sketch, "E183", {"start": v(-4100, -7250) * mm, "end": v(100, -7250) * mm});
            skLineSegment(sketch, "E184", {"start": v(100, -7250) * mm, "end": v(100, -5250) * mm});
            skLineSegment(sketch, "E185", {"start": v(100, -5250) * mm, "end": v(4100, -5250) * mm});
            skPoint(sketch, "E185.endSnap0", {"position": v(4100, -5850) * mm});
            skLineSegment(sketch, "E186", {"start": v(4100, -5250) * mm, "end": v(4100, -3250) * mm});
            skLineSegment(sketch, "E187", {"start": v(4100, -3250) * mm, "end": v(3900, -3250) * mm});
            skLineSegment(sketch, "E188", {"start": v(3900, -3250) * mm, "end": v(3900, -5050) * mm});
            skLineSegment(sketch, "E189", {"start": v(3900, -5050) * mm, "end": v(-100, -5050) * mm});
            skLineSegment(sketch, "E190", {"start": v(-100, -5050) * mm, "end": v(-100, -7050) * mm});
            skLineSegment(sketch, "E191", {"start": v(-100, -7050) * mm, "end": v(-3900, -7050) * mm});
            skLineSegment(sketch, "E192", {"start": v(-3900, -7050) * mm, "end": v(-3900, -3250) * mm});
            skLineSegment(sketch, "E193", {"start": v(-3900, -3250) * mm, "end": v(-4100, -3250) * mm});
            skSolve(sketch);
        }
        {
            var Q0;
            Q0=makeQuery(id+"F20.imprint","IMPRINT",FACE,{"disambiguationData":[TD([[makeQuery(id+"F20.imprint","IMPRINT",EDGE,{"derivedFrom":sQuery(id+"F20.wireOp",EDGE,"E182")}),1.0]])]});
            var Q1;
            {var subQ10=sQuery(id+"F20.wireOp",EDGE,"E183");Q1=makeQuery(id+"F20.imprint","IMPRINT",FACE,{"disambiguationData":[TD([[makeQuery(id+"F20.imprint","IMPRINT",EDGE,{"derivedFrom":subQ10}),1.0]])]});}
            var Q2;
            {var subQ3=sQuery(id+"F20.wireOp",EDGE,"E187");Q2=makeQuery(id+"F20.imprint","IMPRINT",FACE,{"disambiguationData":[TD([[makeQuery(id+"F20.imprint","IMPRINT",EDGE,{"derivedFrom":subQ3}),1.0]])]});}
            extrude(context, id + "F21", {"entities" : qUnion([Q0, Q1, Q2]), "operationType" : NewBodyOperationType.ADD, "depth" : 2200 * mm, "offsetDistance" : 25 * mm});
        }
        {
            var Q0;
            {var subQ3=sQuery(id+"F20.wireOp",EDGE,"E193");Q0=makeQuery(id+"F20.imprint","IMPRINT",FACE,{"disambiguationData":[TD([[makeQuery(id+"F20.imprint","IMPRINT",EDGE,{"derivedFrom":subQ3}),1.0]])]});}
            var Q1;
            {var subQ10=sQuery(id+"F20.wireOp",EDGE,"E183");Q1=makeQuery(id+"F20.imprint","IMPRINT",FACE,{"disambiguationData":[TD([[makeQuery(id+"F20.imprint","IMPRINT",EDGE,{"derivedFrom":subQ10}),1.0]])]});}
            var Q2;
            {var subQ3=sQuery(id+"F20.wireOp",EDGE,"E187");Q2=makeQuery(id+"F20.imprint","IMPRINT",FACE,{"disambiguationData":[TD([[makeQuery(id+"F20.imprint","IMPRINT",EDGE,{"derivedFrom":subQ3}),1.0]])]});}
            extrude(context, id + "F22", {"entities" : qUnion([Q0, Q1, Q2]), "depth" : 2200 * mm, "offsetDistance" : 25 * mm});
        }
        {
            var Q0;
            Q0=qCreatedBy(makeId("Top.planeOp"),FACE);
            cPlane(context, id + "F23", {"entities" : qUnion([Q0]), "cplaneType" : CPlaneType.OFFSET, "offset" : 1300 * mm, "oppositeDirection" : true, "width" : 150 * mm, "height" : 150 * mm});
        }
        {
            var Q0;
            Q0=qCreatedBy(id+"F23.planeOp",FACE);
            var sketch = newSketch(context, id + "F24", { "sketchPlane" : qUnion([Q0])});
            skLineSegment(sketch, "E194.bottom", {"start": v(-10500, 4250) * mm, "end": v(10500, 4250) * mm});
            skLineSegment(sketch, "E194.top", {"start": v(-10500, -22750) * mm, "end": v(10500, -22750) * mm});
            skLineSegment(sketch, "E194.left", {"start": v(-10500, 4250) * mm, "end": v(-10500, -22750) * mm});
            skLineSegment(sketch, "E194.right", {"start": v(10500, 4250) * mm, "end": v(10500, -22750) * mm});
            skLineSegment(sketch, "E195", {"start": v(-4100, 4250) * mm, "end": v(-4100, -4250) * mm});
            skLineSegment(sketch, "E196", {"start": v(-4100, -4250) * mm, "end": v(4100, -4250) * mm});
            skLineSegment(sketch, "E197", {"start": v(4100, -4250) * mm, "end": v(4100, 4250) * mm});
            skSolve(sketch);
        }
        {
            var Q0;
            Q0=makeQuery(id+"F24.imprint","IMPRINT",FACE,{"disambiguationData":[TD([[makeQuery(id+"F24.imprint","IMPRINT",EDGE,{"derivedFrom":sQuery(id+"F24.wireOp",EDGE,"E194.top")}),1.0]])]});
            extrude(context, id + "F25", {"entities" : qUnion([Q0]), "depth" : 100 * mm, "offsetDistance" : 25 * mm});
        }
    });
